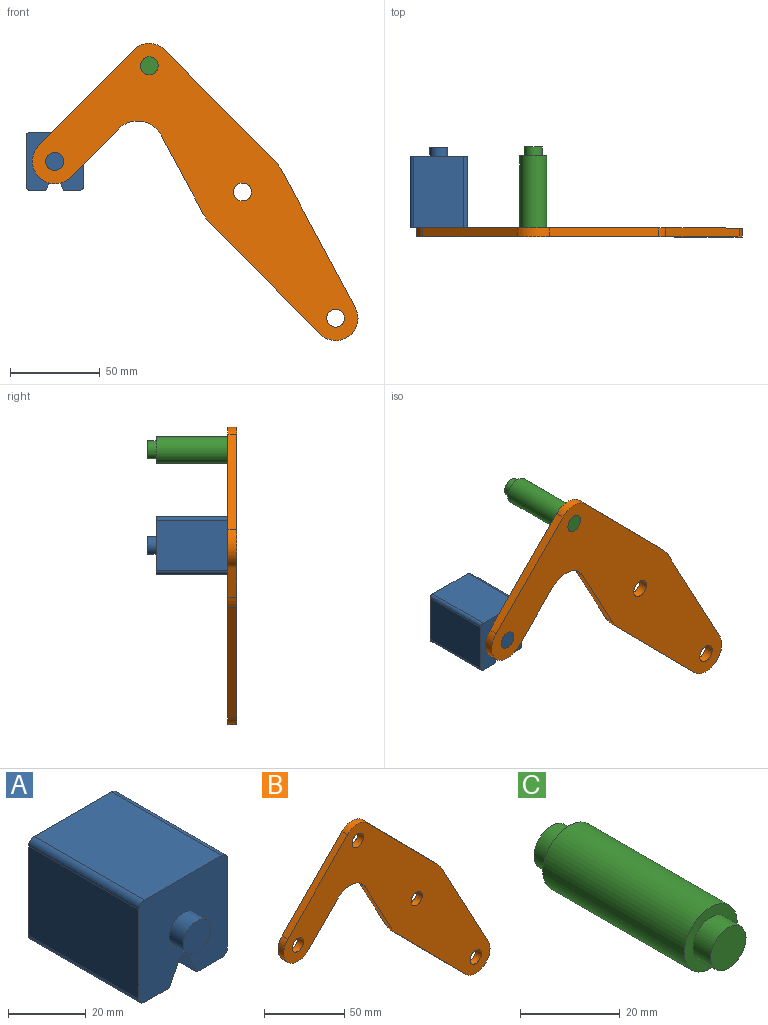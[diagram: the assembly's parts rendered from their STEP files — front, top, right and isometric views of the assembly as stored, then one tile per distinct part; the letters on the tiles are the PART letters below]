
ASSEMBLY  parts=3 mates=1
PART A: 18 faces, bbox 32.1x50x32.1 mm
  f0: plane 40x28.08mm, normal (1,0,0), area 1123.1mm2, adj f4,f10,f13,f14
  f1: plane 40x9.04mm, normal (0,0,-1), area 361.6mm2, adj f2,f4,f10,f14
  f2: plane 40x6.42mm, normal (-0.89,0,-0.45), area 287.2mm2, adj f1,f4,f10,f15
  f3: plane 40x6.42mm, normal (0.89,0,-0.45), area 287.2mm2, adj f4,f5,f10,f15
  f4: plane 32.08x32.08mm, normal (0,-1,0), area 900.6mm2, adj f0,f1,f2,f3,f5,f6,f7,f9
  f5: plane 40x9.04mm, normal (0,0,-1), area 361.6mm2, adj f3,f4,f10,f16
  f6: plane 40x28.08mm, normal (0,0,1), area 1123.1mm2, adj f4,f10,f13,f17
  f7: plane 40x28.08mm, normal (-1,0,0), area 1123.1mm2, adj f4,f10,f16,f17
  f8: plane 10x10mm, normal (0,-1,0), area 78.5mm2, adj f9
  f9: cylinder r=5mm len=10mm, axis (0,1,0), area 157.1mm2, adj f4,f8
  f10: plane 32.08x32.08mm, normal (0,1,0), area 900.6mm2, adj f0,f1,f2,f3,f5,f6,f7,f12
  f11: plane 10x10mm, normal (0,1,0), area 78.5mm2, adj f12
  f12: cylinder r=5mm len=10mm, axis (0,-1,0), area 157.1mm2, adj f10,f11
  f13: cylinder r=2mm len=40mm, axis (0,1,0), area 125.7mm2, adj f0,f4,f6,f10
  f14: cylinder r=2mm len=40mm, axis (0,-1,0), area 125.7mm2, adj f0,f1,f4,f10
  f15: cylinder r=2mm len=40mm, axis (0,1,0), area 177.1mm2, adj f2,f3,f4,f10
  f16: cylinder r=2mm len=40mm, axis (0,1,0), area 125.7mm2, adj f4,f5,f7,f10
  f17: cylinder r=2mm len=40mm, axis (0,-1,0), area 125.7mm2, adj f4,f6,f7,f10
PART B: 18 faces, bbox 181.7x5x165.8 mm
  f0: plane 43.49x23.35mm, normal (-0.88,0,-0.47), area 246.8mm2, adj f1,f14,f16,f17
  f1: cylinder r=25mm len=5.75mm, axis (0,1,0), area 35.8mm2, adj f0,f2,f16,f17
  f2: plane 61.6x60.87mm, normal (-0.71,0,-0.7), area 433mm2, adj f1,f3,f16,f17
  f3: cylinder r=12.5mm len=21.39mm, axis (0,1,0), area 178.4mm2, adj f2,f4,f16,f17
  f4: plane 76.3x40.96mm, normal (0.88,0,0.47), area 433mm2, adj f3,f5,f16,f17
  f5: cylinder r=25mm len=5.75mm, axis (0,1,0), area 35.8mm2, adj f4,f6,f16,f17
  f6: plane 61.6x60.87mm, normal (0.71,0,0.7), area 433mm2, adj f5,f7,f16,f17
  f7: cylinder r=12.5mm len=17.78mm, axis (0,1,0), area 98.9mm2, adj f6,f8,f16,f17
  f8: plane 53.35x52.71mm, normal (-0.71,0,0.7), area 375mm2, adj f7,f9,f16,f17
  f9: cylinder r=12.5mm len=21.39mm, axis (0,1,0), area 196.3mm2, adj f8,f10,f16,f17
  f10: plane 26.86x26.54mm, normal (0.71,0,-0.7), area 188.8mm2, adj f9,f14,f16,f17
  f11: cylinder r=5mm len=10mm, axis (0,1,0), area 157.1mm2, adj f16,f17
  f12: cylinder r=5mm len=10mm, axis (0,1,0), area 157.1mm2, adj f16,f17
  f13: cylinder r=5mm len=10mm, axis (0,1,0), area 157.1mm2, adj f16,f17
  f14: cylinder r=15mm len=23.89mm, axis (0,1,0), area 140.2mm2, adj f0,f10,f16,f17
  f15: cylinder r=5mm len=10mm, axis (0,1,0), area 157.1mm2, adj f16,f17
  f16: plane 181.66x165.78mm, normal (0,-1,0), area 8710.1mm2, adj f0,f1,f2,f3,f4,f5,f6,f7
  f17: plane 181.66x165.78mm, normal (0,1,0), area 8710.1mm2, adj f0,f1,f2,f3,f4,f5,f6,f7
PART C: 7 faces, bbox 15x50x15 mm
  f0: cylinder r=7.5mm len=40mm, axis (0,-1,0), area 1885mm2, adj f2,f5
  f1: cylinder r=5mm len=10mm, axis (0,1,0), area 157.1mm2, adj f2,f3
  f2: plane 15x15mm, normal (0,-1,0), area 98.2mm2, adj f0,f1
  f3: plane 10x10mm, normal (0,-1,0), area 78.5mm2, adj f1
  f4: cylinder r=5mm len=10mm, axis (0,-1,0), area 157.1mm2, adj f5,f6
  f5: plane 15x15mm, normal (0,1,0), area 98.2mm2, adj f0,f4
  f6: plane 10x10mm, normal (0,1,0), area 78.5mm2, adj f4
PLACE A t=(7.48,-19.75,-0.99)mm
PLACE B t=(7.48,-19.75,-0.99)mm fixed
PLACE C t=(7.48,-19.75,-0.99)mm
MATE revolute A.f9 <-> B.f9  axis (0,1,0) through (-97.2,-19.75,16.05)mm
